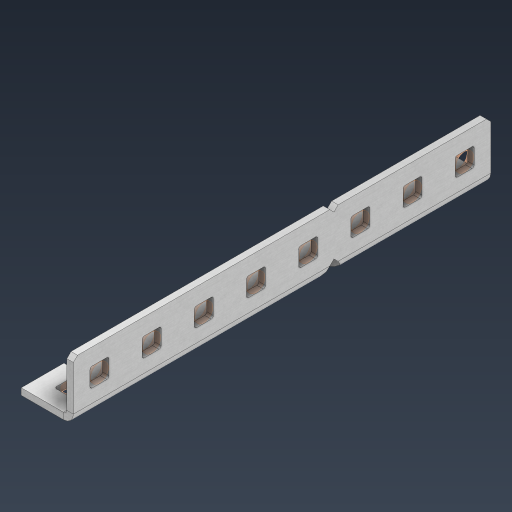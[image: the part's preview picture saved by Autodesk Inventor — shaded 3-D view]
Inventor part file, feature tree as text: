
AUTODESK INVENTOR PART (.ipt)
format: ipt  version: 2024.3 (Build 283343000, 343)  size: 552,960 bytes
history: native  units: in
note: dims shown in document units (in); Inventor stores cm internally (conversion verified against a paired STEP export)
features: other x31, extrude x22, sheet_metal_op x11, pattern_linear x2, mirror x1, chamfer x1, sketch x1
ambient origin geometry x8: Origin, YZ Plane, XZ Plane, XY Plane, X Axis, Y Axis, Z Axis, Center Point
bodies: Solid1 (feature_tree), Body (feature_tree)
feature tree (69):
  sheet_metal_op  "Flanges"
  other  "Flange Pattern Plane"
  other  "Flange Pattern Sketch"
  sheet_metal_op  "Flange Pattern"
  sheet_metal_op  "Body Pattern"
  pattern_linear  "Center Pattern"  Spacing1=4.0in  [1 undecoded]
  other  "Arc Length"
  mirror  "Notch Mirror"
  pattern_linear  "Notch Pattern"  Spacing1=0.0625in  [1 undecoded]
  chamfer  "End Chamfer"
  extrude  "Half Cut"  Depth=0.0625in
  other  "Plate1"
  sketch  "Sketch2"  dims[d0=1.0in d1=4.0in d2=0.0625in d3=0.0625in d4=0.0312in d5=0.125in d6=0.0625in d7=0.5in d8=90.0deg d9=0.0312in d10=0.25in d11=0.0625in d12=0.0625in d16=0.182in d17=0.02in d18=0.0625in d19=0.0in d20=0.25in d21=0.25in d38=3.1496in d40=0.5in d41=0.3937in d43=1.0in d46=0.172in d47=1.0in d48=0.0in d49=0.182in d50=0.02in d51=0.25in d52=0.25in d53=0.0625in d54=0.0in d55=0.172in d56=1.0in d57=0.0in d58=0.25in d60=3.1496in d62=0.5in d63=0.3937in d65=0.5in d85=0.1473in d86=0.1782in d88=0.04in d89=0.0625in d90=0.0in d91=0.04in d92=0.0491in d95=2.5in d96=0.04in d97=0.25in d98=45.0deg d99=0.25in d100=0.5in d101=0.0in d102=2.497in d106=0.182in d107=0.02in d108=0.5in d109=0.5in d110=0.0625in d111=0.0in d112=0.172in d113=0.5in d114=0.0in d117=0.5in d118=0.5in d119=0.5in]
  other  "Plate2"
  sheet_metal_op  "Bend1"
  sheet_metal_op  "Corner1"
  other  "Srf1"
  other  "Srf2"
  other  "Srf91"
  sheet_metal_op  "Body Pattern Sketch"
  other  "Srf92"
  other  "Srf786"
  other  "Srf823"
  other  "Srf824"
  other  "Srf825"
  other  "Srf826"
  other  "Srf827"
  other  "Srf828"
  other  "Srf856"
  other  "Srf857"
  other  "Srf858"
  other  "Srf859"
  other  "Srf860"
  other  "Srf861"
  other  "Srf889"
  other  "Srf890"
  other  "Srf891"
  other  "Srf892"
  other  "Srf893"
  other  "Srf894"
  other  "Srf895"
  sheet_metal_op  "Flange Stamp"
  sheet_metal_op  "Flange Circle"
  sheet_metal_op  "Body Stamp"
  sheet_metal_op  "Body Circle"
  other  "Center Stamp"
  other  "Center Circle"
  sheet_metal_op  "Notch"
  extrude  "ExtrusionSrf2"  Depth=0.5in
  extrude  "ExtrusionSrf92"  Depth=0.5in
  extrude  "ExtrusionSrf823"  Depth=0.0625in
  extrude  "ExtrusionSrf824"  Depth=0.5in TaperAngle=90.0deg
  extrude  "ExtrusionSrf825"  Depth=0.25in
  extrude  "ExtrusionSrf826"  Depth=0.0625in
  extrude  "ExtrusionSrf827"  Depth=0.0625in
  extrude  "ExtrusionSrf828"  Depth=0.182in
  extrude  "ExtrusionSrf856"  Depth=0.02in
  extrude  "ExtrusionSrf857"  Depth=0.0625in
  extrude  "ExtrusionSrf858"  TaperAngle=0.0deg  [1 undecoded]
  extrude  "ExtrusionSrf859"  Depth=0.25in
  extrude  "ExtrusionSrf860"  Depth=0.25in
  extrude  "ExtrusionSrf861"  Depth=0.5in
  extrude  "ExtrusionSrf889"  Depth=0.5in
  extrude  "ExtrusionSrf890"  Depth=1.0in TaperAngle=0.0deg
  extrude  "ExtrusionSrf891"  Depth=0.182in
  extrude  "ExtrusionSrf892"  Depth=0.02in
  extrude  "ExtrusionSrf893"  Depth=0.25in
  extrude  "ExtrusionSrf894"  Depth=0.25in
  extrude  "ExtrusionSrf895"  Depth=0.0625in
note: 3 required parameter values undecoded (feature->parameter linkage not recoverable at this tier; creation-order binding heuristic only, values carry confidence <= 0.55)
